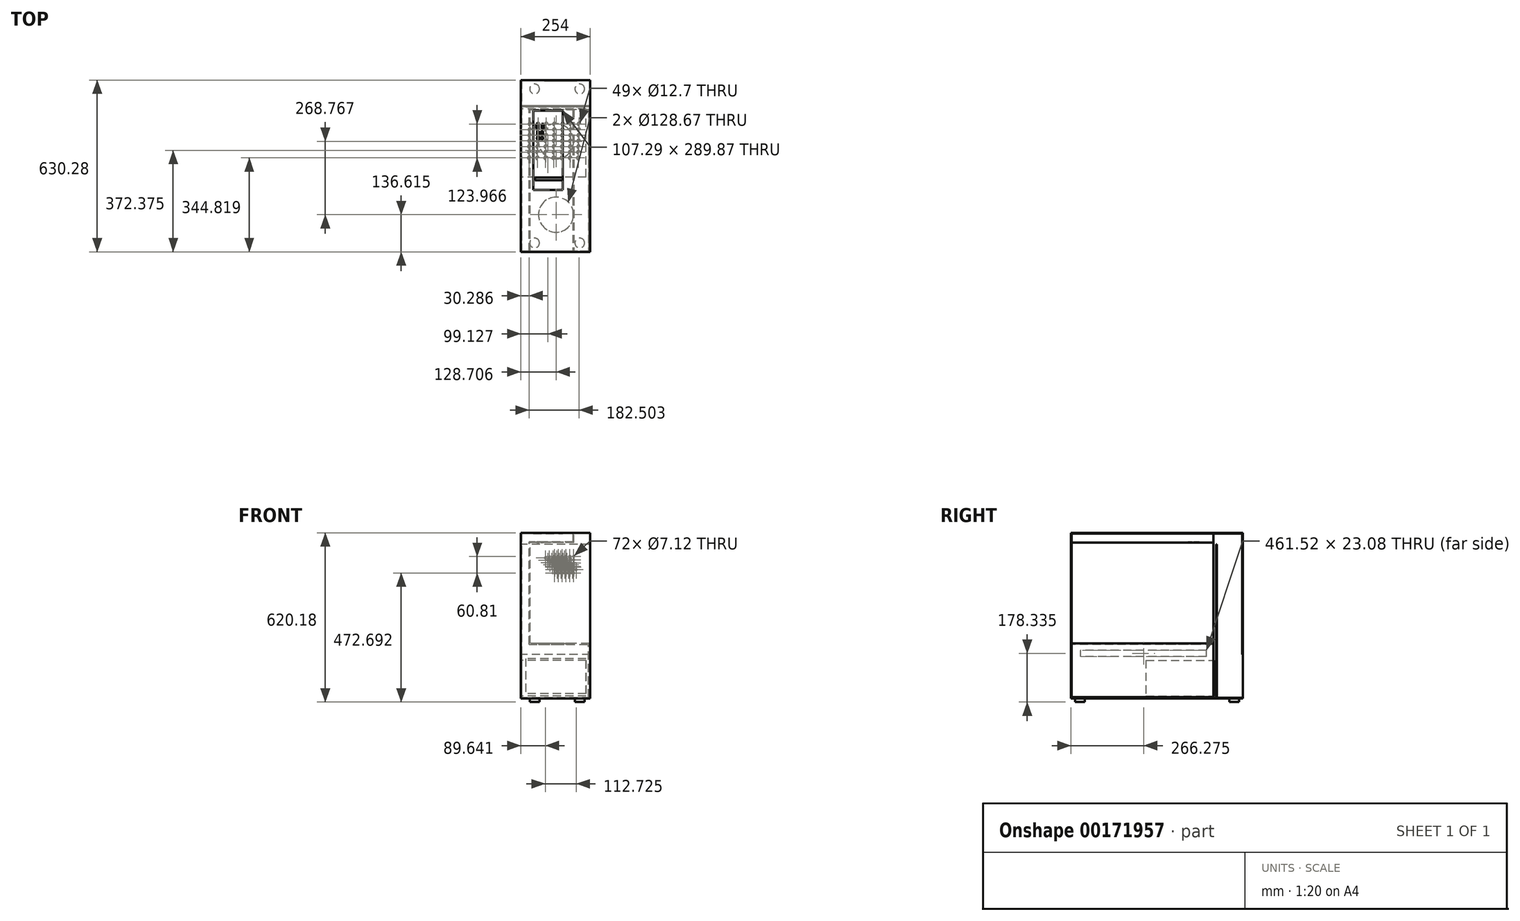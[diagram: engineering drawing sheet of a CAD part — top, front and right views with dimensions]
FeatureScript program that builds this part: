
annotation { "Feature Type Name" : "Feature", "Feature Type Description" : "" }
export const myFeature = defineFeature(function(context is Context, id is Id, definition is map)
    precondition{}
    {
        {
            var Q0;
            Q0=qCreatedBy(makeId("Right.planeOp"),FACE);
            var sketch = newSketch(context, id + "F0", { "sketchPlane" : qUnion([Q0])});
            skLineSegment(sketch, "E0.bottom", {"start": v(257.34, 162.25) * mm, "end": v(-372.94, 162.25) * mm});
            skLineSegment(sketch, "E0.top", {"start": v(257.34, -445.23) * mm, "end": v(-372.94, -445.23) * mm});
            skLineSegment(sketch, "E0.left", {"start": v(257.34, 162.25) * mm, "end": v(257.34, -283.43) * mm});
            skLineSegment(sketch, "E0.right", {"start": v(-372.94, 162.25) * mm, "end": v(-372.94, -445.23) * mm});
            skLineSegment(sketch, "E1.0", {"start": v(254.8, 159.7) * mm, "end": v(-370.4, 159.7) * mm});
            skLineSegment(sketch, "E1.1", {"start": v(254.8, 159.7) * mm, "end": v(254.8, -283.43) * mm});
            skLineSegment(sketch, "E1.2", {"start": v(254.8, -442.69) * mm, "end": v(-370.4, -442.69) * mm});
            skLineSegment(sketch, "E1.3", {"start": v(-370.4, 159.7) * mm, "end": v(-370.4, -442.69) * mm});
            skLineSegment(sketch, "E2", {"start": v(254.8, -283.43) * mm, "end": v(257.34, -283.43) * mm});
            skLineSegment(sketch, "E3", {"start": v(254.8, -442.69) * mm, "end": v(257.34, -445.23) * mm});
            skLineSegment(sketch, "E4", {"start": v(254.8, -283.43) * mm, "end": v(254.8, -442.69) * mm});
            skLineSegment(sketch, "E5", {"start": v(257.34, -283.43) * mm, "end": v(257.34, -445.23) * mm});
            skLineSegment(sketch, "E6", {"start": v(158.54, 119.69) * mm, "end": v(158.54, -442.69) * mm});
            skLineSegment(sketch, "E7", {"start": v(162.12, -442.69) * mm, "end": v(162.12, 119.69) * mm});
            skLineSegment(sketch, "E8", {"start": v(158.54, 119.69) * mm, "end": v(162.12, 119.69) * mm});
            skSolve(sketch);
        }
        {
            var Q0;
            Q0=makeQuery(id+"F0.imprint","IMPRINT",FACE,{"disambiguationData":[TD([[makeQuery(id+"F0.imprint","IMPRINT",EDGE,{"derivedFrom":sQuery(id+"F0.wireOp",EDGE,"E0.bottom")}),1.0]])]});
            var Q1;
            {var subQ0=sQuery(id+"F0.wireOp",EDGE,"E6");Q1=makeQuery(id+"F0.imprint","IMPRINT",FACE,{"disambiguationData":[TD([[makeQuery(id+"F0.imprint","IMPRINT",EDGE,{"derivedFrom":subQ0}),1.0]])]});}
            extrude(context, id + "F1", {"entities" : qUnion([Q0, Q1]), "depth" : 254 * mm});
        }
        {
            var Q0;
            Q0=makeQuery(id+"F0.imprint","IMPRINT",FACE,{"disambiguationData":[TD([[makeQuery(id+"F0.imprint","IMPRINT",EDGE,{"derivedFrom":sQuery(id+"F0.wireOp",EDGE,"E1.0")}),1.0]])]});
            var Q1;
            Q1=makeQuery(id+"F0.imprint","IMPRINT",FACE,{"disambiguationData":[TD([[makeQuery(id+"F0.imprint","IMPRINT",EDGE,{"derivedFrom":sQuery(id+"F0.wireOp",EDGE,"E2")}),-1.0]])]});
            extrude(context, id + "F2", {"entities" : qUnion([Q0, Q1]), "operationType" : NewBodyOperationType.ADD, "depth" : 2.54 * mm});
        }
        {
            var Q0;
            Q0=makeQuery(id+"F1.opExtrude","SWEPT_FACE",FACE,{"disambiguationData":[OSD([sQuery(id+"F0.wireOp",EDGE,"E0.top")])]});
            var sketch = newSketch(context, id + "F3", { "sketchPlane" : qUnion([Q0])});
            skCircle(sketch, "E9", {"center": v(212.79, -95.85) * mm, "radius": 6.35 * mm});
            skCircle(sketch, "E10.0.1.0", {"center": v(212.34, -75.18) * mm, "radius": 6.35 * mm});
            skCircle(sketch, "E10.0.2.0", {"center": v(211.9, -54.52) * mm, "radius": 6.35 * mm});
            skCircle(sketch, "E10.0.3.0", {"center": v(211.45, -33.86) * mm, "radius": 6.35 * mm});
            skCircle(sketch, "E10.0.4.0", {"center": v(211, -13.2) * mm, "radius": 6.35 * mm});
            skCircle(sketch, "E10.0.5.0", {"center": v(210.56, 7.46) * mm, "radius": 6.35 * mm});
            skCircle(sketch, "E10.0.6.0", {"center": v(210.12, 28.12) * mm, "radius": 6.35 * mm});
            skCircle(sketch, "E10.1.0.0", {"center": v(182.82, -95.85) * mm, "radius": 6.35 * mm});
            skCircle(sketch, "E10.1.1.0", {"center": v(182.37, -75.18) * mm, "radius": 6.35 * mm});
            skCircle(sketch, "E10.1.2.0", {"center": v(181.93, -54.52) * mm, "radius": 6.35 * mm});
            skCircle(sketch, "E10.1.3.0", {"center": v(181.48, -33.86) * mm, "radius": 6.35 * mm});
            skCircle(sketch, "E10.1.4.0", {"center": v(181.04, -13.2) * mm, "radius": 6.35 * mm});
            skCircle(sketch, "E10.1.5.0", {"center": v(180.6, 7.46) * mm, "radius": 6.35 * mm});
            skCircle(sketch, "E10.1.6.0", {"center": v(180.15, 28.12) * mm, "radius": 6.35 * mm});
            skCircle(sketch, "E10.2.0.0", {"center": v(152.85, -95.85) * mm, "radius": 6.35 * mm});
            skCircle(sketch, "E10.2.1.0", {"center": v(152.4, -75.18) * mm, "radius": 6.35 * mm});
            skCircle(sketch, "E10.2.2.0", {"center": v(151.95, -54.52) * mm, "radius": 6.35 * mm});
            skCircle(sketch, "E10.2.3.0", {"center": v(151.5, -33.86) * mm, "radius": 6.35 * mm});
            skCircle(sketch, "E10.2.4.0", {"center": v(151.06, -13.2) * mm, "radius": 6.35 * mm});
            skCircle(sketch, "E10.2.5.0", {"center": v(150.62, 7.46) * mm, "radius": 6.35 * mm});
            skCircle(sketch, "E10.2.6.0", {"center": v(150.17, 28.12) * mm, "radius": 6.35 * mm});
            skCircle(sketch, "E10.3.0.0", {"center": v(122.87, -95.85) * mm, "radius": 6.35 * mm});
            skCircle(sketch, "E10.3.1.0", {"center": v(122.43, -75.18) * mm, "radius": 6.35 * mm});
            skCircle(sketch, "E10.3.2.0", {"center": v(121.98, -54.52) * mm, "radius": 6.35 * mm});
            skCircle(sketch, "E10.3.3.0", {"center": v(121.54, -33.86) * mm, "radius": 6.35 * mm});
            skCircle(sketch, "E10.3.4.0", {"center": v(121.1, -13.2) * mm, "radius": 6.35 * mm});
            skCircle(sketch, "E10.3.5.0", {"center": v(120.65, 7.46) * mm, "radius": 6.35 * mm});
            skCircle(sketch, "E10.3.6.0", {"center": v(120.2, 28.12) * mm, "radius": 6.35 * mm});
            skCircle(sketch, "E10.4.0.0", {"center": v(92.9, -95.85) * mm, "radius": 6.35 * mm});
            skCircle(sketch, "E10.4.1.0", {"center": v(92.46, -75.18) * mm, "radius": 6.35 * mm});
            skCircle(sketch, "E10.4.2.0", {"center": v(92.01, -54.52) * mm, "radius": 6.35 * mm});
            skCircle(sketch, "E10.4.3.0", {"center": v(91.57, -33.86) * mm, "radius": 6.35 * mm});
            skCircle(sketch, "E10.4.4.0", {"center": v(91.12, -13.2) * mm, "radius": 6.35 * mm});
            skCircle(sketch, "E10.4.5.0", {"center": v(90.68, 7.46) * mm, "radius": 6.35 * mm});
            skCircle(sketch, "E10.4.6.0", {"center": v(90.23, 28.12) * mm, "radius": 6.35 * mm});
            skCircle(sketch, "E10.5.0.0", {"center": v(62.93, -95.85) * mm, "radius": 6.35 * mm});
            skCircle(sketch, "E10.5.1.0", {"center": v(62.48, -75.18) * mm, "radius": 6.35 * mm});
            skCircle(sketch, "E10.5.2.0", {"center": v(62.04, -54.52) * mm, "radius": 6.35 * mm});
            skCircle(sketch, "E10.5.3.0", {"center": v(61.6, -33.86) * mm, "radius": 6.35 * mm});
            skCircle(sketch, "E10.5.4.0", {"center": v(61.15, -13.2) * mm, "radius": 6.35 * mm});
            skCircle(sketch, "E10.5.5.0", {"center": v(60.7, 7.46) * mm, "radius": 6.35 * mm});
            skCircle(sketch, "E10.5.6.0", {"center": v(60.26, 28.12) * mm, "radius": 6.35 * mm});
            skCircle(sketch, "E10.6.0.0", {"center": v(32.96, -95.85) * mm, "radius": 6.35 * mm});
            skCircle(sketch, "E10.6.1.0", {"center": v(32.51, -75.18) * mm, "radius": 6.35 * mm});
            skCircle(sketch, "E10.6.2.0", {"center": v(32.07, -54.52) * mm, "radius": 6.35 * mm});
            skCircle(sketch, "E10.6.3.0", {"center": v(31.62, -33.86) * mm, "radius": 6.35 * mm});
            skCircle(sketch, "E10.6.4.0", {"center": v(31.18, -13.2) * mm, "radius": 6.35 * mm});
            skCircle(sketch, "E10.6.5.0", {"center": v(30.73, 7.46) * mm, "radius": 6.35 * mm});
            skCircle(sketch, "E10.6.6.0", {"center": v(30.29, 28.12) * mm, "radius": 6.35 * mm});
            skLineSegment(sketch, "E10.direction1", {"start": v(212.79, -95.85) * mm, "end": v(182.82, -95.85) * mm, "construction": true});
            skLineSegment(sketch, "E10.direction2", {"start": v(212.79, -95.85) * mm, "end": v(212.34, -75.18) * mm, "construction": true});
            skSolve(sketch);
        }
        {
            var Q0;
            Q0 = qSketchRegion(id + "F3", true);
            extrude(context, id + "F4", {"entities" : qUnion([Q0]), "operationType" : NewBodyOperationType.REMOVE, "endBound" : BoundingType.UP_TO_NEXT, "oppositeDirection" : true, "depth" : 25.4 * mm});
        }
        {
            var Q0;
            Q0=makeQuery(id+"F1.opExtrude","SWEPT_FACE",FACE,{"disambiguationData":[OSD([sQuery(id+"F0.wireOp",EDGE,"E7")])]});
            var sketch = newSketch(context, id + "F5", { "sketchPlane" : qUnion([Q0])});
            skLineSegment(sketch, "E11.0", {"start": v(-254, -283.43) * mm, "end": v(-2.54, -283.43) * mm});
            skLineSegment(sketch, "E11.1", {"start": v(-254, -442.69) * mm, "end": v(-2.54, -442.69) * mm});
            skLineSegment(sketch, "E11.2", {"start": v(-2.54, -283.43) * mm, "end": v(-2.54, -442.69) * mm});
            skLineSegment(sketch, "E11.3", {"start": v(-254, -442.69) * mm, "end": v(-254, -283.43) * mm});
            skPoint(sketch, "E12.orphan", {"position": v(-254, 119.69) * mm});
            skPoint(sketch, "E13.orphan", {"position": v(-2.54, -445.23) * mm});
            skLineSegment(sketch, "E14.0", {"start": v(-238.76, -427.45) * mm, "end": v(-17.78, -427.45) * mm});
            skLineSegment(sketch, "E14.1", {"start": v(-238.76, -427.45) * mm, "end": v(-238.76, -298.67) * mm});
            skLineSegment(sketch, "E14.2", {"start": v(-238.76, -298.67) * mm, "end": v(-17.78, -298.67) * mm});
            skLineSegment(sketch, "E14.3", {"start": v(-17.78, -298.67) * mm, "end": v(-17.78, -427.45) * mm});
            skSolve(sketch);
        }
        {
            var Q0;
            Q0=makeQuery(id+"F5.imprint","IMPRINT",FACE,{"disambiguationData":[TD([[makeQuery(id+"F5.imprint","IMPRINT",EDGE,{"derivedFrom":sQuery(id+"F5.wireOp",EDGE,"E14.0")}),1.0]])]});
            extrude(context, id + "F6", {"entities" : qUnion([Q0]), "operationType" : NewBodyOperationType.REMOVE, "endBound" : BoundingType.UP_TO_NEXT, "oppositeDirection" : true, "depth" : 25.4 * mm});
        }
        {
            var Q0;
            Q0=makeQuery(id+"F2.opExtrude","CAP_FACE",FACE,{"disambiguationData":[OSD([sQuery(id+"F0.wireOp",EDGE,"E1.0"),sQuery(id+"F0.wireOp",EDGE,"E1.1"),sQuery(id+"F0.wireOp",EDGE,"E1.2"),sQuery(id+"F0.wireOp",EDGE,"E1.3"),sQuery(id+"F0.wireOp",EDGE,"E2"),sQuery(id+"F0.wireOp",EDGE,"E3"),sQuery(id+"F0.wireOp",EDGE,"E5"),sQuery(id+"F0.wireOp",EDGE,"E6"),sQuery(id+"F0.wireOp",EDGE,"E7"),sQuery(id+"F0.wireOp",EDGE,"E8")])],"isStart":false});
            var sketch = newSketch(context, id + "F7", { "sketchPlane" : qUnion([Q0])});
            skLineSegment(sketch, "E15.bottom", {"start": v(-98.6, -304.81) * mm, "end": v(151.54, -304.81) * mm});
            skLineSegment(sketch, "E15.top", {"start": v(-98.6, -436.03) * mm, "end": v(151.54, -436.03) * mm});
            skLineSegment(sketch, "E15.left", {"start": v(-98.6, -304.81) * mm, "end": v(-98.6, -436.03) * mm});
            skLineSegment(sketch, "E15.right", {"start": v(151.54, -304.81) * mm, "end": v(151.54, -436.03) * mm});
            skSolve(sketch);
        }
        {
            var Q0;
            Q0 = qSketchRegion(id + "F7", true);
            extrude(context, id + "F8", {"entities" : qUnion([Q0]), "operationType" : NewBodyOperationType.ADD, "depth" : 236.22 * mm});
        }
        {
            var Q0;
            Q0=makeQuery(id+"F1.opExtrude","SWEPT_FACE",FACE,{"disambiguationData":[OSD([sQuery(id+"F0.wireOp",EDGE,"E1.0")])]});
            var sketch = newSketch(context, id + "F9", { "sketchPlane" : qUnion([Q0])});
            skLineSegment(sketch, "E16.bottom", {"start": v(29.78, 370.4) * mm, "end": v(34.16, 370.4) * mm});
            skLineSegment(sketch, "E16.top", {"start": v(29.78, -149.4) * mm, "end": v(34.16, -149.4) * mm});
            skLineSegment(sketch, "E16.left", {"start": v(29.78, 370.4) * mm, "end": v(29.78, -149.4) * mm});
            skLineSegment(sketch, "E16.right", {"start": v(34.16, 370.4) * mm, "end": v(34.16, -149.4) * mm});
            skSolve(sketch);
        }
        {
            var Q0;
            Q0 = qSketchRegion(id + "F9", true);
            extrude(context, id + "F10", {"entities" : qUnion([Q0]), "operationType" : NewBodyOperationType.ADD, "depth" : 406.4 * mm, "hasSecondDirection" : true, "secondDirectionOppositeDirection" : false, "secondDirectionDepth" : 30.48 * mm, "offsetDistance" : 25.4 * mm});
        }
        {
            var Q0;
            Q0=makeQuery(id+"F10.opExtrude","SWEPT_FACE",FACE,{"disambiguationData":[OSD([sQuery(id+"F9.wireOp",EDGE,"E16.right")])]});
            var sketch = newSketch(context, id + "F11", { "sketchPlane" : qUnion([Q0])});
            skLineSegment(sketch, "E17.0", {"start": v(-370.4, -246.7) * mm, "end": v(149.4, -246.7) * mm});
            skLineSegment(sketch, "E18", {"start": v(-370.4, -246.7) * mm, "end": v(-370.4, -243.52) * mm});
            skLineSegment(sketch, "E19", {"start": v(-370.4, -243.52) * mm, "end": v(149.4, -243.52) * mm});
            skLineSegment(sketch, "E20", {"start": v(149.4, -243.52) * mm, "end": v(149.4, -246.7) * mm});
            skSolve(sketch);
        }
        {
            var Q0;
            Q0=makeQuery(id+"F11.imprint","IMPRINT",FACE,{"disambiguationData":[TD([[makeQuery(id+"F11.imprint","IMPRINT",EDGE,{"derivedFrom":sQuery(id+"F11.wireOp",EDGE,"E17.0")}),1.0]])]});
            extrude(context, id + "F12", {"entities" : qUnion([Q0]), "operationType" : NewBodyOperationType.ADD, "depth" : 215.9 * mm, "offsetDistance" : 25.4 * mm});
        }
        {
            var Q0;
            Q0=makeQuery(id+"F2.opExtrude","CAP_FACE",FACE,{"disambiguationData":[OSD([sQuery(id+"F0.wireOp",EDGE,"E1.0"),sQuery(id+"F0.wireOp",EDGE,"E1.1"),sQuery(id+"F0.wireOp",EDGE,"E1.2"),sQuery(id+"F0.wireOp",EDGE,"E1.3"),sQuery(id+"F0.wireOp",EDGE,"E2"),sQuery(id+"F0.wireOp",EDGE,"E3"),sQuery(id+"F0.wireOp",EDGE,"E5"),sQuery(id+"F0.wireOp",EDGE,"E6"),sQuery(id+"F0.wireOp",EDGE,"E7"),sQuery(id+"F0.wireOp",EDGE,"E8")])],"isStart":false});
            var sketch = newSketch(context, id + "F13", { "sketchPlane" : qUnion([Q0])});
            skLineSegment(sketch, "E21.bottom", {"start": v(-337.42, -268.06) * mm, "end": v(124.1, -268.06) * mm});
            skLineSegment(sketch, "E21.top", {"start": v(-337.42, -291.13) * mm, "end": v(124.1, -291.13) * mm});
            skLineSegment(sketch, "E21.left", {"start": v(-337.42, -268.06) * mm, "end": v(-337.42, -291.13) * mm});
            skLineSegment(sketch, "E21.right", {"start": v(124.1, -268.06) * mm, "end": v(124.1, -291.13) * mm});
            skSolve(sketch);
        }
        {
            var Q0;
            Q0 = qSketchRegion(id + "F13", true);
            extrude(context, id + "F14", {"entities" : qUnion([Q0]), "operationType" : NewBodyOperationType.REMOVE, "endBound" : BoundingType.UP_TO_NEXT, "oppositeDirection" : true, "depth" : 25.4 * mm, "offsetDistance" : 25.4 * mm});
        }
        {
            var Q0;
            Q0=makeQuery(id+"F12.boolean.opBoolean","MERGE",FACE,{"derivedFrom":[makeQuery(id+"F10.opExtrude","CAP_FACE",FACE,{"disambiguationData":[OSD([sQuery(id+"F9.wireOp",EDGE,"E16.bottom"),sQuery(id+"F9.wireOp",EDGE,"E16.top"),sQuery(id+"F9.wireOp",EDGE,"E16.left"),sQuery(id+"F9.wireOp",EDGE,"E16.right")])],"isStart":false}),makeQuery(id+"F12.opExtrude","SWEPT_FACE",FACE,{"disambiguationData":[OSD([sQuery(id+"F11.wireOp",EDGE,"E17.0")])]})]});
            var sketch = newSketch(context, id + "F15", { "sketchPlane" : qUnion([Q0])});
            skCircle(sketch, "E22", {"center": v(128.7, 236.33) * mm, "radius": 64.34 * mm});
            skLineSegment(sketch, "E23", {"start": v(128.7, 236.33) * mm, "end": v(128.7, -32.44) * mm, "construction": true});
            skCircle(sketch, "E24", {"center": v(128.7, -32.44) * mm, "radius": 64.34 * mm});
            skSolve(sketch);
        }
        {
            var Q0;
            Q0 = qSketchRegion(id + "F15", true);
            extrude(context, id + "F16", {"entities" : qUnion([Q0]), "operationType" : NewBodyOperationType.REMOVE, "endBound" : BoundingType.UP_TO_NEXT, "oppositeDirection" : true, "depth" : 25.4 * mm, "offsetDistance" : 25.4 * mm});
        }
        {
            var Q0;
            Q0=makeQuery(id+"F1.opExtrude","SWEPT_FACE",FACE,{"disambiguationData":[OSD([sQuery(id+"F0.wireOp",EDGE,"E0.top")])]});
            var sketch = newSketch(context, id + "F17", { "sketchPlane" : qUnion([Q0])});
            skCircle(sketch, "E25", {"center": v(215.43, 340.2) * mm, "radius": 17.78 * mm});
            skCircle(sketch, "E26", {"center": v(50.14, 340.2) * mm, "radius": 17.78 * mm});
            skLineSegment(sketch, "E27", {"start": v(50.14, 340.2) * mm, "end": v(215.43, 340.2) * mm, "construction": true});
            skLineSegment(sketch, "E28", {"start": v(254, 57.8) * mm, "end": v(32.7, 57.8) * mm, "construction": true});
            skPoint(sketch, "E28.endSnap0", {"position": v(254, 57.8) * mm});
            skCircle(sketch, "E29.MirrorC", {"center": v(50.14, -224.6) * mm, "radius": 17.78 * mm});
            skCircle(sketch, "E30.MirrorC", {"center": v(215.43, -224.6) * mm, "radius": 17.78 * mm});
            skSolve(sketch);
        }
        {
            var Q0;
            Q0 = qSketchRegion(id + "F17", true);
            extrude(context, id + "F18", {"entities" : qUnion([Q0]), "operationType" : NewBodyOperationType.ADD, "depth" : 12.7 * mm});
        }
        {
            var Q0;
            Q0=makeQuery(id+"F10.opExtrude","SWEPT_FACE",FACE,{"disambiguationData":[OSD([sQuery(id+"F9.wireOp",EDGE,"E16.right")])]});
            var sketch = newSketch(context, id + "F19", { "sketchPlane" : qUnion([Q0])});
            skLineSegment(sketch, "E31.0", {"start": v(-370.4, 129.23) * mm, "end": v(149.4, 129.23) * mm});
            skLineSegment(sketch, "E32", {"start": v(-370.4, 129.23) * mm, "end": v(-370.4, 126.05) * mm});
            skLineSegment(sketch, "E33", {"start": v(-370.4, 126.05) * mm, "end": v(149.4, 126.05) * mm});
            skLineSegment(sketch, "E34", {"start": v(149.4, 126.05) * mm, "end": v(149.4, 129.23) * mm});
            skSolve(sketch);
        }
        {
            var Q0;
            Q0=makeQuery(id+"F19.imprint","IMPRINT",FACE,{"disambiguationData":[TD([[makeQuery(id+"F19.imprint","IMPRINT",EDGE,{"derivedFrom":sQuery(id+"F19.wireOp",EDGE,"E31.0")}),-1.0]])]});
            extrude(context, id + "F20", {"entities" : qUnion([Q0]), "operationType" : NewBodyOperationType.ADD, "depth" : 159.26 * mm, "offsetDistance" : 25.4 * mm});
        }
        {
            var Q0;
            Q0=makeQuery(id+"F20.boolean.opBoolean","MERGE",FACE,{"derivedFrom":[makeQuery(id+"F10.opExtrude","CAP_FACE",FACE,{"disambiguationData":[OSD([sQuery(id+"F9.wireOp",EDGE,"E16.bottom"),sQuery(id+"F9.wireOp",EDGE,"E16.top"),sQuery(id+"F9.wireOp",EDGE,"E16.left"),sQuery(id+"F9.wireOp",EDGE,"E16.right")])],"isStart":true}),makeQuery(id+"F20.opExtrude","SWEPT_FACE",FACE,{"disambiguationData":[OSD([sQuery(id+"F19.wireOp",EDGE,"E31.0")])]})]});
            var sketch = newSketch(context, id + "F21", { "sketchPlane" : qUnion([Q0])});
            skLineSegment(sketch, "E35.0", {"start": v(193.42, -370.4) * mm, "end": v(193.42, 149.4) * mm});
            skLineSegment(sketch, "E36", {"start": v(193.42, -370.4) * mm, "end": v(190.24, -370.4) * mm});
            skLineSegment(sketch, "E37", {"start": v(190.24, -370.4) * mm, "end": v(190.24, 149.4) * mm});
            skLineSegment(sketch, "E38", {"start": v(190.24, 149.4) * mm, "end": v(193.42, 149.4) * mm});
            skSolve(sketch);
        }
        {
            var Q0;
            Q0 = qSketchRegion(id + "F21", true);
            extrude(context, id + "F22", {"entities" : qUnion([Q0]), "operationType" : NewBodyOperationType.ADD, "endBound" : BoundingType.UP_TO_NEXT, "depth" : 25.4 * mm, "offsetDistance" : 25.4 * mm});
        }
        {
            var Q0;
            Q0=makeQuery(id+"F1.opExtrude","SWEPT_FACE",FACE,{"disambiguationData":[OSD([sQuery(id+"F0.wireOp",EDGE,"E0.bottom")])]});
            var sketch = newSketch(context, id + "F23", { "sketchPlane" : qUnion([Q0])});
            skLineSegment(sketch, "E39.bottom", {"start": v(45.48, 144.37) * mm, "end": v(152.77, 144.37) * mm});
            skLineSegment(sketch, "E39.top", {"start": v(45.48, -145.5) * mm, "end": v(152.77, -145.5) * mm});
            skLineSegment(sketch, "E39.left", {"start": v(45.48, 144.37) * mm, "end": v(45.48, -145.5) * mm});
            skLineSegment(sketch, "E39.right", {"start": v(152.77, 144.37) * mm, "end": v(152.77, -145.5) * mm});
            skSolve(sketch);
        }
        {
            var Q0;
            Q0 = qSketchRegion(id + "F23", true);
            extrude(context, id + "F24", {"entities" : qUnion([Q0]), "operationType" : NewBodyOperationType.REMOVE, "endBound" : BoundingType.UP_TO_NEXT, "oppositeDirection" : true, "depth" : 25.4 * mm, "offsetDistance" : 25.4 * mm});
        }
        {
            var Q0;
            Q0=makeQuery(id+"F20.boolean.opBoolean","MERGE",FACE,{"derivedFrom":[makeQuery(id+"F10.opExtrude","CAP_FACE",FACE,{"disambiguationData":[OSD([sQuery(id+"F9.wireOp",EDGE,"E16.bottom"),sQuery(id+"F9.wireOp",EDGE,"E16.top"),sQuery(id+"F9.wireOp",EDGE,"E16.left"),sQuery(id+"F9.wireOp",EDGE,"E16.right")])],"isStart":true}),makeQuery(id+"F20.opExtrude","SWEPT_FACE",FACE,{"disambiguationData":[OSD([sQuery(id+"F19.wireOp",EDGE,"E31.0")])]})]});
            var sketch = newSketch(context, id + "F25", { "sketchPlane" : qUnion([Q0])});
            skLineSegment(sketch, "E40.bottom", {"start": v(75.18, 96.66) * mm, "end": v(83.12, 96.66) * mm});
            skLineSegment(sketch, "E40.top", {"start": v(75.18, 78.34) * mm, "end": v(83.12, 78.34) * mm});
            skLineSegment(sketch, "E40.left", {"start": v(75.18, 96.66) * mm, "end": v(75.18, 78.34) * mm});
            skLineSegment(sketch, "E40.right", {"start": v(83.12, 96.66) * mm, "end": v(83.12, 78.34) * mm});
            skLineSegment(sketch, "E41.bottom", {"start": v(73.95, 69.79) * mm, "end": v(80.67, 69.79) * mm});
            skLineSegment(sketch, "E41.top", {"start": v(73.95, 56.35) * mm, "end": v(80.67, 56.35) * mm});
            skLineSegment(sketch, "E41.left", {"start": v(73.95, 69.79) * mm, "end": v(73.95, 56.35) * mm});
            skLineSegment(sketch, "E41.right", {"start": v(80.67, 69.79) * mm, "end": v(80.67, 56.35) * mm});
            skCircle(sketch, "E42", {"center": v(77, 44.13) * mm, "radius": 4.96 * mm});
            skLineSegment(sketch, "E43.bottom", {"start": v(55.94, 96.65) * mm, "end": v(63.88, 96.65) * mm});
            skLineSegment(sketch, "E43.top", {"start": v(55.94, 78.33) * mm, "end": v(63.88, 78.33) * mm});
            skLineSegment(sketch, "E43.left", {"start": v(55.94, 96.65) * mm, "end": v(55.94, 78.33) * mm});
            skLineSegment(sketch, "E43.right", {"start": v(63.88, 96.65) * mm, "end": v(63.88, 78.33) * mm});
            skCircle(sketch, "E44", {"center": v(63.18, 44.17) * mm, "radius": 4.96 * mm});
            skLineSegment(sketch, "E45.bottom", {"start": v(59.47, 70.09) * mm, "end": v(66.2, 70.09) * mm});
            skLineSegment(sketch, "E45.top", {"start": v(59.47, 56.65) * mm, "end": v(66.2, 56.65) * mm});
            skLineSegment(sketch, "E45.left", {"start": v(59.47, 70.09) * mm, "end": v(59.47, 56.65) * mm});
            skLineSegment(sketch, "E45.right", {"start": v(66.2, 70.09) * mm, "end": v(66.2, 56.65) * mm});
            skLineSegment(sketch, "E46.bottom", {"start": v(51.1, -110.28) * mm, "end": v(155.38, -110.28) * mm});
            skLineSegment(sketch, "E46.top", {"start": v(51.1, -100.15) * mm, "end": v(155.38, -100.15) * mm});
            skLineSegment(sketch, "E46.left", {"start": v(51.1, -110.28) * mm, "end": v(51.1, -100.15) * mm});
            skLineSegment(sketch, "E46.right", {"start": v(155.38, -110.28) * mm, "end": v(155.38, -100.15) * mm});
            skSolve(sketch);
        }
        {
            var Q0;
            Q0 = qSketchRegion(id + "F25", true);
            extrude(context, id + "F26", {"entities" : qUnion([Q0]), "operationType" : NewBodyOperationType.REMOVE, "endBound" : BoundingType.UP_TO_NEXT, "oppositeDirection" : true, "depth" : 25.4 * mm, "offsetDistance" : 25.4 * mm});
        }
        {
            var Q0;
            Q0=makeQuery(id+"F1.opExtrude","SWEPT_FACE",FACE,{"disambiguationData":[OSD([sQuery(id+"F0.wireOp",EDGE,"E6")])]});
            var sketch = newSketch(context, id + "F27", { "sketchPlane" : qUnion([Q0])});
            skCircle(sketch, "E47", {"center": v(123.17, 14.76) * mm, "radius": 3.56 * mm});
            skCircle(sketch, "E48.0.1.0", {"center": v(123.19, 26.92) * mm, "radius": 3.56 * mm});
            skCircle(sketch, "E48.0.2.0", {"center": v(123.21, 39.09) * mm, "radius": 3.56 * mm});
            skCircle(sketch, "E48.0.3.0", {"center": v(123.23, 51.25) * mm, "radius": 3.56 * mm});
            skCircle(sketch, "E48.0.4.0", {"center": v(123.26, 63.41) * mm, "radius": 3.56 * mm});
            skCircle(sketch, "E48.0.5.0", {"center": v(123.28, 75.57) * mm, "radius": 3.56 * mm});
            skCircle(sketch, "E48.1.0.0", {"center": v(137.14, 14.76) * mm, "radius": 3.56 * mm});
            skCircle(sketch, "E48.1.1.0", {"center": v(137.16, 26.92) * mm, "radius": 3.56 * mm});
            skCircle(sketch, "E48.1.2.0", {"center": v(137.18, 39.09) * mm, "radius": 3.56 * mm});
            skCircle(sketch, "E48.1.3.0", {"center": v(137.2, 51.25) * mm, "radius": 3.56 * mm});
            skCircle(sketch, "E48.1.4.0", {"center": v(137.23, 63.41) * mm, "radius": 3.56 * mm});
            skCircle(sketch, "E48.1.5.0", {"center": v(137.25, 75.57) * mm, "radius": 3.56 * mm});
            skCircle(sketch, "E48.2.0.0", {"center": v(151.1, 14.76) * mm, "radius": 3.56 * mm});
            skCircle(sketch, "E48.2.1.0", {"center": v(151.13, 26.92) * mm, "radius": 3.56 * mm});
            skCircle(sketch, "E48.2.2.0", {"center": v(151.15, 39.09) * mm, "radius": 3.56 * mm});
            skCircle(sketch, "E48.2.3.0", {"center": v(151.17, 51.25) * mm, "radius": 3.56 * mm});
            skCircle(sketch, "E48.2.4.0", {"center": v(151.2, 63.41) * mm, "radius": 3.56 * mm});
            skCircle(sketch, "E48.2.5.0", {"center": v(151.22, 75.57) * mm, "radius": 3.56 * mm});
            skCircle(sketch, "E48.3.0.0", {"center": v(165.08, 14.76) * mm, "radius": 3.56 * mm});
            skCircle(sketch, "E48.3.1.0", {"center": v(165.1, 26.92) * mm, "radius": 3.56 * mm});
            skCircle(sketch, "E48.3.2.0", {"center": v(165.12, 39.09) * mm, "radius": 3.56 * mm});
            skCircle(sketch, "E48.3.3.0", {"center": v(165.14, 51.25) * mm, "radius": 3.56 * mm});
            skCircle(sketch, "E48.3.4.0", {"center": v(165.17, 63.41) * mm, "radius": 3.56 * mm});
            skCircle(sketch, "E48.3.5.0", {"center": v(165.19, 75.57) * mm, "radius": 3.56 * mm});
            skCircle(sketch, "E48.4.0.0", {"center": v(179.05, 14.76) * mm, "radius": 3.56 * mm});
            skCircle(sketch, "E48.4.1.0", {"center": v(179.07, 26.92) * mm, "radius": 3.56 * mm});
            skCircle(sketch, "E48.4.2.0", {"center": v(179.1, 39.09) * mm, "radius": 3.56 * mm});
            skCircle(sketch, "E48.4.3.0", {"center": v(179.11, 51.25) * mm, "radius": 3.56 * mm});
            skCircle(sketch, "E48.4.4.0", {"center": v(179.14, 63.41) * mm, "radius": 3.56 * mm});
            skCircle(sketch, "E48.4.5.0", {"center": v(179.16, 75.57) * mm, "radius": 3.56 * mm});
            skCircle(sketch, "E48.5.0.0", {"center": v(193.02, 14.76) * mm, "radius": 3.56 * mm});
            skCircle(sketch, "E48.5.1.0", {"center": v(193.04, 26.92) * mm, "radius": 3.56 * mm});
            skCircle(sketch, "E48.5.2.0", {"center": v(193.06, 39.09) * mm, "radius": 3.56 * mm});
            skCircle(sketch, "E48.5.3.0", {"center": v(193.08, 51.25) * mm, "radius": 3.56 * mm});
            skCircle(sketch, "E48.5.4.0", {"center": v(193.1, 63.41) * mm, "radius": 3.56 * mm});
            skCircle(sketch, "E48.5.5.0", {"center": v(193.13, 75.57) * mm, "radius": 3.56 * mm});
            skLineSegment(sketch, "E48.direction1", {"start": v(123.17, 14.76) * mm, "end": v(137.14, 14.76) * mm, "construction": true});
            skLineSegment(sketch, "E48.direction2", {"start": v(123.17, 14.76) * mm, "end": v(123.19, 26.92) * mm, "construction": true});
            skSolve(sketch);
        }
        {
            var Q0;
            Q0 = qSketchRegion(id + "F27", true);
            extrude(context, id + "F28", {"entities" : qUnion([Q0]), "operationType" : NewBodyOperationType.REMOVE, "endBound" : BoundingType.UP_TO_NEXT, "oppositeDirection" : true, "depth" : 25.4 * mm, "offsetDistance" : 25.4 * mm});
        }
        {
            var Q0;
            Q0=makeQuery(id+"F1.opExtrude","SWEPT_FACE",FACE,{"disambiguationData":[OSD([sQuery(id+"F0.wireOp",EDGE,"E1.1")])]});
            var sketch = newSketch(context, id + "F29", { "sketchPlane" : qUnion([Q0])});
            skCircle(sketch, "E49", {"center": v(89.64, 70.42) * mm, "radius": 3.56 * mm});
            skCircle(sketch, "E50.0.1.0", {"center": v(98.22, 61.8) * mm, "radius": 3.56 * mm});
            skCircle(sketch, "E50.0.2.0", {"center": v(106.8, 53.17) * mm, "radius": 3.56 * mm});
            skCircle(sketch, "E50.0.3.0", {"center": v(115.37, 44.55) * mm, "radius": 3.56 * mm});
            skCircle(sketch, "E50.0.4.0", {"center": v(123.94, 35.92) * mm, "radius": 3.56 * mm});
            skCircle(sketch, "E50.0.5.0", {"center": v(132.52, 27.3) * mm, "radius": 3.56 * mm});
            skCircle(sketch, "E50.1.0.0", {"center": v(103.61, 70.42) * mm, "radius": 3.56 * mm});
            skCircle(sketch, "E50.1.1.0", {"center": v(112.19, 61.8) * mm, "radius": 3.56 * mm});
            skCircle(sketch, "E50.1.2.0", {"center": v(120.76, 53.17) * mm, "radius": 3.56 * mm});
            skCircle(sketch, "E50.1.3.0", {"center": v(129.34, 44.55) * mm, "radius": 3.56 * mm});
            skCircle(sketch, "E50.1.4.0", {"center": v(137.91, 35.92) * mm, "radius": 3.56 * mm});
            skCircle(sketch, "E50.1.5.0", {"center": v(146.49, 27.3) * mm, "radius": 3.56 * mm});
            skCircle(sketch, "E50.2.0.0", {"center": v(117.58, 70.42) * mm, "radius": 3.56 * mm});
            skCircle(sketch, "E50.2.1.0", {"center": v(126.16, 61.8) * mm, "radius": 3.56 * mm});
            skCircle(sketch, "E50.2.2.0", {"center": v(134.73, 53.17) * mm, "radius": 3.56 * mm});
            skCircle(sketch, "E50.2.3.0", {"center": v(143.3, 44.55) * mm, "radius": 3.56 * mm});
            skCircle(sketch, "E50.2.4.0", {"center": v(151.88, 35.92) * mm, "radius": 3.56 * mm});
            skCircle(sketch, "E50.2.5.0", {"center": v(160.46, 27.3) * mm, "radius": 3.56 * mm});
            skCircle(sketch, "E50.3.0.0", {"center": v(131.55, 70.42) * mm, "radius": 3.56 * mm});
            skCircle(sketch, "E50.3.1.0", {"center": v(140.13, 61.8) * mm, "radius": 3.56 * mm});
            skCircle(sketch, "E50.3.2.0", {"center": v(148.7, 53.17) * mm, "radius": 3.56 * mm});
            skCircle(sketch, "E50.3.3.0", {"center": v(157.28, 44.55) * mm, "radius": 3.56 * mm});
            skCircle(sketch, "E50.3.4.0", {"center": v(165.85, 35.92) * mm, "radius": 3.56 * mm});
            skCircle(sketch, "E50.3.5.0", {"center": v(174.43, 27.3) * mm, "radius": 3.56 * mm});
            skCircle(sketch, "E50.4.0.0", {"center": v(145.52, 70.42) * mm, "radius": 3.56 * mm});
            skCircle(sketch, "E50.4.1.0", {"center": v(154.1, 61.8) * mm, "radius": 3.56 * mm});
            skCircle(sketch, "E50.4.2.0", {"center": v(162.67, 53.17) * mm, "radius": 3.56 * mm});
            skCircle(sketch, "E50.4.3.0", {"center": v(171.25, 44.55) * mm, "radius": 3.56 * mm});
            skCircle(sketch, "E50.4.4.0", {"center": v(179.82, 35.92) * mm, "radius": 3.56 * mm});
            skCircle(sketch, "E50.4.5.0", {"center": v(188.4, 27.3) * mm, "radius": 3.56 * mm});
            skCircle(sketch, "E50.5.0.0", {"center": v(159.5, 70.42) * mm, "radius": 3.56 * mm});
            skCircle(sketch, "E50.5.1.0", {"center": v(168.07, 61.8) * mm, "radius": 3.56 * mm});
            skCircle(sketch, "E50.5.2.0", {"center": v(176.64, 53.17) * mm, "radius": 3.56 * mm});
            skCircle(sketch, "E50.5.3.0", {"center": v(185.22, 44.55) * mm, "radius": 3.56 * mm});
            skCircle(sketch, "E50.5.4.0", {"center": v(193.8, 35.92) * mm, "radius": 3.56 * mm});
            skCircle(sketch, "E50.5.5.0", {"center": v(202.37, 27.3) * mm, "radius": 3.56 * mm});
            skLineSegment(sketch, "E50.direction1", {"start": v(89.64, 70.42) * mm, "end": v(103.61, 70.42) * mm, "construction": true});
            skLineSegment(sketch, "E50.direction2", {"start": v(89.64, 70.42) * mm, "end": v(98.22, 61.8) * mm, "construction": true});
            skSolve(sketch);
        }
        {
            var Q0;
            Q0 = qSketchRegion(id + "F29", true);
            extrude(context, id + "F30", {"entities" : qUnion([Q0]), "operationType" : NewBodyOperationType.REMOVE, "endBound" : BoundingType.UP_TO_NEXT, "oppositeDirection" : true, "depth" : 25.4 * mm, "offsetDistance" : 25.4 * mm});
        }
        {
            var Q0;
            Q0=makeQuery(id+"F12.boolean.opBoolean","MERGE",FACE,{"derivedFrom":[makeQuery(id+"F10.opExtrude","CAP_FACE",FACE,{"disambiguationData":[OSD([sQuery(id+"F9.wireOp",EDGE,"E16.bottom"),sQuery(id+"F9.wireOp",EDGE,"E16.top"),sQuery(id+"F9.wireOp",EDGE,"E16.left"),sQuery(id+"F9.wireOp",EDGE,"E16.right")])],"isStart":false}),makeQuery(id+"F12.opExtrude","SWEPT_FACE",FACE,{"disambiguationData":[OSD([sQuery(id+"F11.wireOp",EDGE,"E17.0")])]})]});
            var sketch = newSketch(context, id + "F31", { "sketchPlane" : qUnion([Q0])});
            skLineSegment(sketch, "E51.0", {"start": v(250.06, 370.4) * mm, "end": v(250.06, -149.4) * mm});
            skLineSegment(sketch, "E52", {"start": v(250.06, -149.4) * mm, "end": v(246.89, -149.4) * mm});
            skLineSegment(sketch, "E53", {"start": v(246.89, -149.4) * mm, "end": v(246.89, 370.4) * mm});
            skLineSegment(sketch, "E54", {"start": v(246.89, 370.4) * mm, "end": v(250.06, 370.4) * mm});
            skSolve(sketch);
        }
        {
            var Q0;
            Q0 = qSketchRegion(id + "F31", true);
            extrude(context, id + "F32", {"entities" : qUnion([Q0]), "operationType" : NewBodyOperationType.ADD, "depth" : 193.55 * mm, "offsetDistance" : 25.4 * mm});
        }
    });
